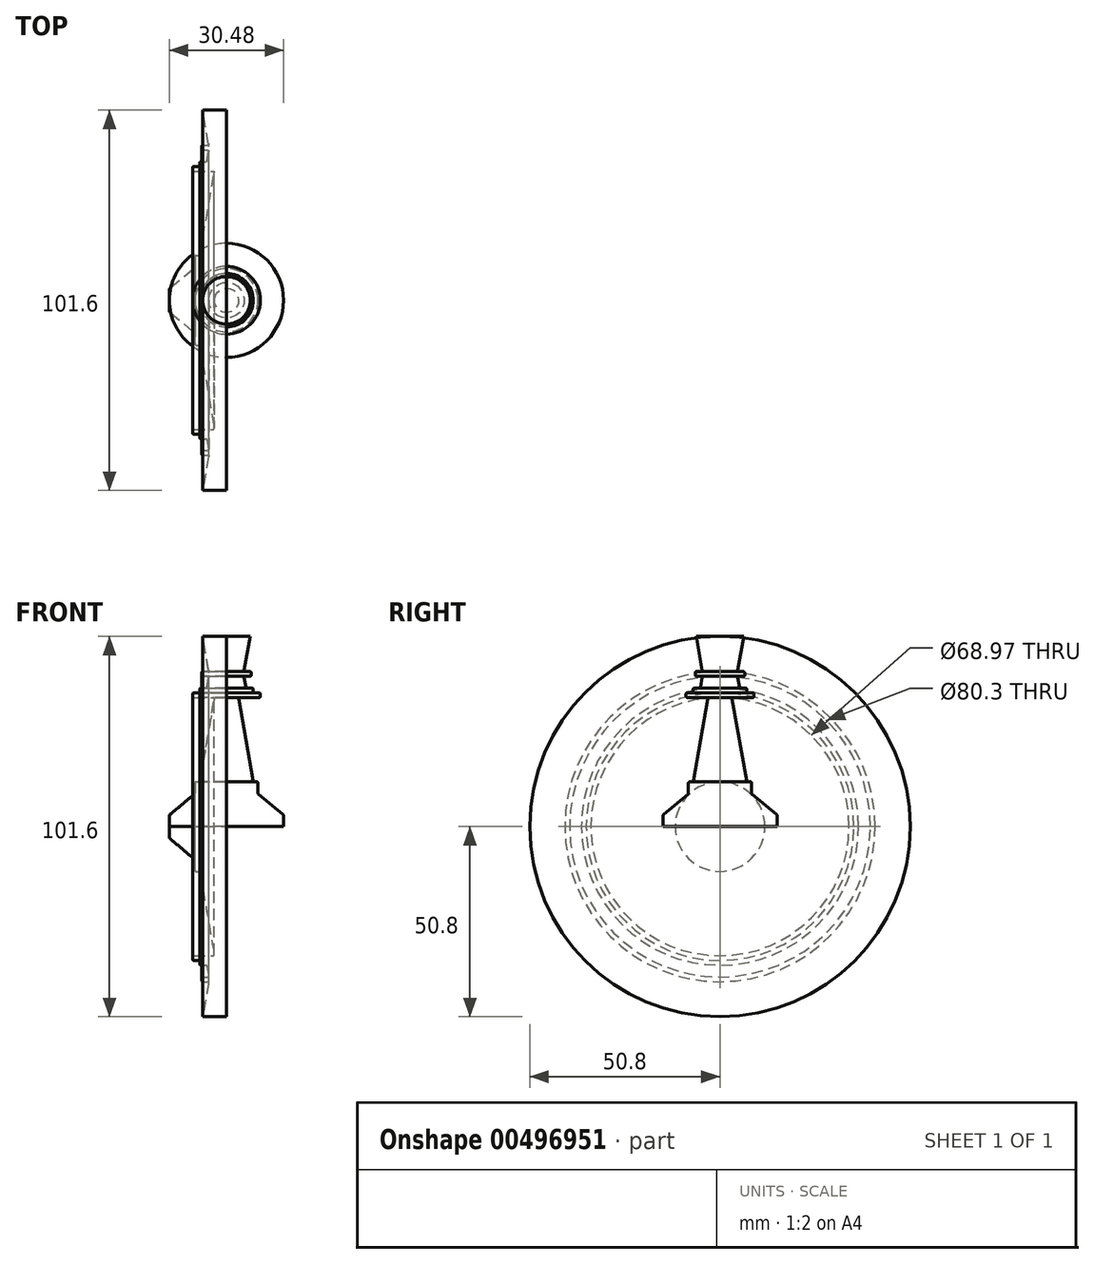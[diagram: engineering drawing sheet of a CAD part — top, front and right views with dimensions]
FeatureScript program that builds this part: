
annotation { "Feature Type Name" : "Feature", "Feature Type Description" : "" }
export const myFeature = defineFeature(function(context is Context, id is Id, definition is map)
    precondition{}
    {
        {
            var Q0;
            Q0=qCreatedBy(makeId("Front.planeOp"),FACE);
            var sketch = newSketch(context, id + "F0", { "sketchPlane" : qUnion([Q0])});
            skLineSegment(sketch, "E0.bottom", {"start": v(0, 0) * mm, "end": v(-15.24, 0) * mm});
            skLineSegment(sketch, "E0.top", {"start": v(0, 50.8) * mm, "end": v(-6.35, 50.8) * mm});
            skLineSegment(sketch, "E0.left", {"start": v(0, 0) * mm, "end": v(0, 50.8) * mm});
            skLineSegment(sketch, "E1", {"start": v(-15.24, 0) * mm, "end": v(-15.24, 2.93) * mm});
            skLineSegment(sketch, "E2", {"start": v(-15.13, 3.18) * mm, "end": v(-8.54, 8.7) * mm});
            skLineSegment(sketch, "E3", {"start": v(-8.43, 8.94) * mm, "end": v(-8.43, 11.65) * mm});
            skLineSegment(sketch, "E4", {"start": v(-8.11, 11.97) * mm, "end": v(-7.43, 11.97) * mm});
            skLineSegment(sketch, "E5", {"start": v(-7.11, 12.23) * mm, "end": v(-3.26, 34.11) * mm});
            skLineSegment(sketch, "E6", {"start": v(-3.57, 34.48) * mm, "end": v(-8.74, 34.48) * mm});
            skLineSegment(sketch, "E7", {"start": v(-9.06, 34.8) * mm, "end": v(-9.06, 35.44) * mm});
            skLineSegment(sketch, "E8", {"start": v(-8.74, 35.75) * mm, "end": v(-7.47, 35.75) * mm});
            skLineSegment(sketch, "E9", {"start": v(-7.15, 36.07) * mm, "end": v(-7.15, 36.7) * mm});
            skLineSegment(sketch, "E10", {"start": v(-6.83, 37.02) * mm, "end": v(-5.51, 37.02) * mm});
            skLineSegment(sketch, "E11", {"start": v(-5.2, 37.29) * mm, "end": v(-4.76, 39.78) * mm});
            skLineSegment(sketch, "E12", {"start": v(-5.07, 40.15) * mm, "end": v(-6.28, 40.15) * mm});
            skLineSegment(sketch, "E13", {"start": v(-6.6, 40.47) * mm, "end": v(-6.6, 41.1) * mm});
            skLineSegment(sketch, "E14", {"start": v(-6.28, 41.42) * mm, "end": v(-5.07, 41.42) * mm});
            skLineSegment(sketch, "E15", {"start": v(-4.76, 41.8) * mm, "end": v(-6.35, 50.8) * mm});
            skPoint(sketch, "E16.visualSharp", {"position": v(-15.24, 3.08) * mm});
            skArc(sketch, "E16.filletArc", {"start": v(-15.13, 3.18) * mm, "mid": v(-15.21, 3.07) * mm, "end": v(-15.24, 2.93) * mm});
            skPoint(sketch, "E17.visualSharp", {"position": v(-8.43, 8.8) * mm});
            skArc(sketch, "E17.filletArc", {"start": v(-8.54, 8.7) * mm, "mid": v(-8.46, 8.8) * mm, "end": v(-8.43, 8.94) * mm});
            skPoint(sketch, "E18.visualSharp", {"position": v(-3.2, 34.48) * mm});
            skArc(sketch, "E18.filletArc", {"start": v(-3.26, 34.11) * mm, "mid": v(-3.33, 34.37) * mm, "end": v(-3.57, 34.48) * mm});
            skPoint(sketch, "E19.visualSharp", {"position": v(-8.43, 11.97) * mm});
            skArc(sketch, "E19.filletArc", {"start": v(-8.11, 11.97) * mm, "mid": v(-8.34, 11.88) * mm, "end": v(-8.43, 11.65) * mm});
            skPoint(sketch, "E20.visualSharp", {"position": v(-7.16, 11.97) * mm});
            skArc(sketch, "E20.filletArc", {"start": v(-7.43, 11.97) * mm, "mid": v(-7.22, 12.04) * mm, "end": v(-7.11, 12.23) * mm});
            skPoint(sketch, "E21.visualSharp", {"position": v(-9.06, 34.48) * mm});
            skArc(sketch, "E21.filletArc", {"start": v(-9.06, 34.8) * mm, "mid": v(-8.96, 34.58) * mm, "end": v(-8.74, 34.48) * mm});
            skPoint(sketch, "E22.visualSharp", {"position": v(-9.06, 35.75) * mm});
            skArc(sketch, "E22.filletArc", {"start": v(-8.74, 35.75) * mm, "mid": v(-8.96, 35.66) * mm, "end": v(-9.06, 35.44) * mm});
            skPoint(sketch, "E23.visualSharp", {"position": v(-7.15, 35.75) * mm});
            skArc(sketch, "E23.filletArc", {"start": v(-7.47, 35.75) * mm, "mid": v(-7.25, 35.85) * mm, "end": v(-7.15, 36.07) * mm});
            skPoint(sketch, "E24.visualSharp", {"position": v(-7.15, 37.02) * mm});
            skArc(sketch, "E24.filletArc", {"start": v(-6.83, 37.02) * mm, "mid": v(-7.06, 36.93) * mm, "end": v(-7.15, 36.7) * mm});
            skPoint(sketch, "E25.visualSharp", {"position": v(-5.25, 37.02) * mm});
            skArc(sketch, "E25.filletArc", {"start": v(-5.51, 37.02) * mm, "mid": v(-5.3, 37.1) * mm, "end": v(-5.2, 37.29) * mm});
            skPoint(sketch, "E26.visualSharp", {"position": v(-4.7, 40.15) * mm});
            skArc(sketch, "E26.filletArc", {"start": v(-4.76, 39.78) * mm, "mid": v(-4.83, 40.04) * mm, "end": v(-5.07, 40.15) * mm});
            skPoint(sketch, "E27.visualSharp", {"position": v(-6.6, 40.15) * mm});
            skArc(sketch, "E27.filletArc", {"start": v(-6.6, 40.47) * mm, "mid": v(-6.5, 40.24) * mm, "end": v(-6.28, 40.15) * mm});
            skPoint(sketch, "E28.visualSharp", {"position": v(-6.6, 41.42) * mm});
            skArc(sketch, "E28.filletArc", {"start": v(-6.28, 41.42) * mm, "mid": v(-6.5, 41.33) * mm, "end": v(-6.6, 41.1) * mm});
            skPoint(sketch, "E29.visualSharp", {"position": v(-4.7, 41.42) * mm});
            skArc(sketch, "E29.filletArc", {"start": v(-5.07, 41.42) * mm, "mid": v(-4.83, 41.53) * mm, "end": v(-4.76, 41.8) * mm});
            skSolve(sketch);
        }
        {
            var Q0;
            Q0 = qSketchRegion(id + "F0", true);
            var Q1;
            Q1=sQuery(id+"F0.wireOp",EDGE,"E0.bottom");
            revolve(context, id + "F1", {"entities" : qUnion([Q0]), "axis" : qUnion([Q1]), "revolveType" : RevolveType.FULL});
        }
        {
            var Q0;
            Q0=makeQuery(id+"F0.imprint","IMPRINT",FACE,{"disambiguationData":[TD([[makeQuery(id+"F0.imprint","IMPRINT",EDGE,{"derivedFrom":sQuery(id+"F0.wireOp",EDGE,"E0.bottom")}),-1.0]])]});
            var Q1;
            Q1=sQuery(id+"F0.wireOp",EDGE,"E0.left");
            revolve(context, id + "F2", {"entities" : qUnion([Q0]), "axis" : qUnion([Q1]), "revolveType" : RevolveType.FULL});
        }
    });
